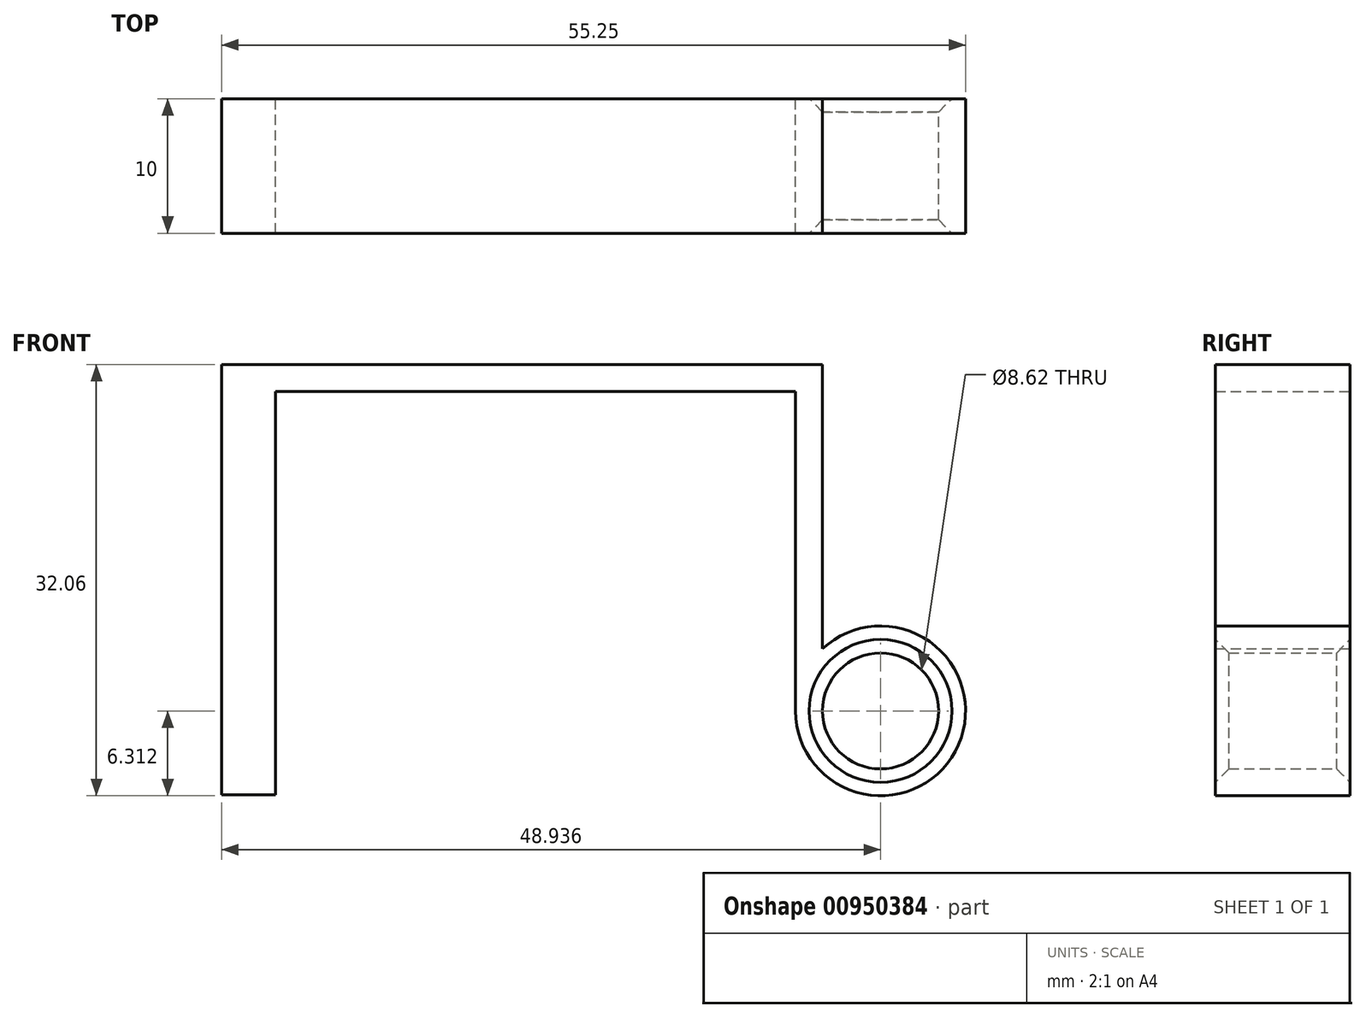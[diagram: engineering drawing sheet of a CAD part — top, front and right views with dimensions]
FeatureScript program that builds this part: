
annotation { "Feature Type Name" : "Feature", "Feature Type Description" : "" }
export const myFeature = defineFeature(function(context is Context, id is Id, definition is map)
    precondition{}
    {
        {
            var Q0;
            Q0=qCreatedBy(makeId("Front.planeOp"),FACE);
            var sketch = newSketch(context, id + "F0", { "sketchPlane" : qUnion([Q0])});
            skLineSegment(sketch, "E0", {"start": v(-16.68, 0) * mm, "end": v(-16.68, 30) * mm});
            skLineSegment(sketch, "E1", {"start": v(-16.68, 30) * mm, "end": v(21.95, 30) * mm});
            skLineSegment(sketch, "E2", {"start": v(21.95, 30) * mm, "end": v(21.95, 6.25) * mm});
            skLineSegment(sketch, "E3", {"start": v(23.95, 10.86) * mm, "end": v(23.95, 32) * mm});
            skLineSegment(sketch, "E4", {"start": v(23.95, 32) * mm, "end": v(-20.68, 32) * mm});
            skLineSegment(sketch, "E5", {"start": v(-20.68, 32) * mm, "end": v(-20.68, 0) * mm});
            skLineSegment(sketch, "E6", {"start": v(-20.68, 0) * mm, "end": v(-16.68, 0) * mm});
            skArc(sketch, "E7", {"start": v(21.95, 6.25) * mm, "mid": v(34.04, 3.74) * mm, "end": v(23.95, 10.86) * mm});
            skCircle(sketch, "E8", {"center": v(28.26, 6.25) * mm, "radius": 4.3 * mm});
            skLineSegment(sketch, "E9", {"start": v(28.26, 6.25) * mm, "end": v(21.95, 6.25) * mm, "construction": true});
            skPoint(sketch, "E10.start.orphan", {"position": v(21.95, 0) * mm});
            skSolve(sketch);
        }
        {
            var Q0;
            Q0=makeQuery(id+"F0.imprint","IMPRINT",FACE,{"disambiguationData":[TD([[makeQuery(id+"F0.imprint","IMPRINT",EDGE,{"derivedFrom":sQuery(id+"F0.wireOp",EDGE,"E0")}),1.0]])]});
            extrude(context, id + "F1", {"entities" : qUnion([Q0]), "depth" : 10 * mm, "offsetDistance" : 25 * mm});
        }
        {
            var Q0;
            Q0=makeQuery(id+"F1.opExtrude","CAP_EDGE",EDGE,{"disambiguationData":[OSD([sQuery(id+"F0.wireOp",EDGE,"E8")])],"isStart":false});
            var Q1;
            Q1=makeQuery(id+"F1.opExtrude","CAP_EDGE",EDGE,{"disambiguationData":[OSD([sQuery(id+"F0.wireOp",EDGE,"E8")])],"isStart":true});
            chamfer(context, id + "F2", {"entities" : qUnion([Q0, Q1]), "width" : 1 * mm, "tangentPropagation" : true});
        }
    });
